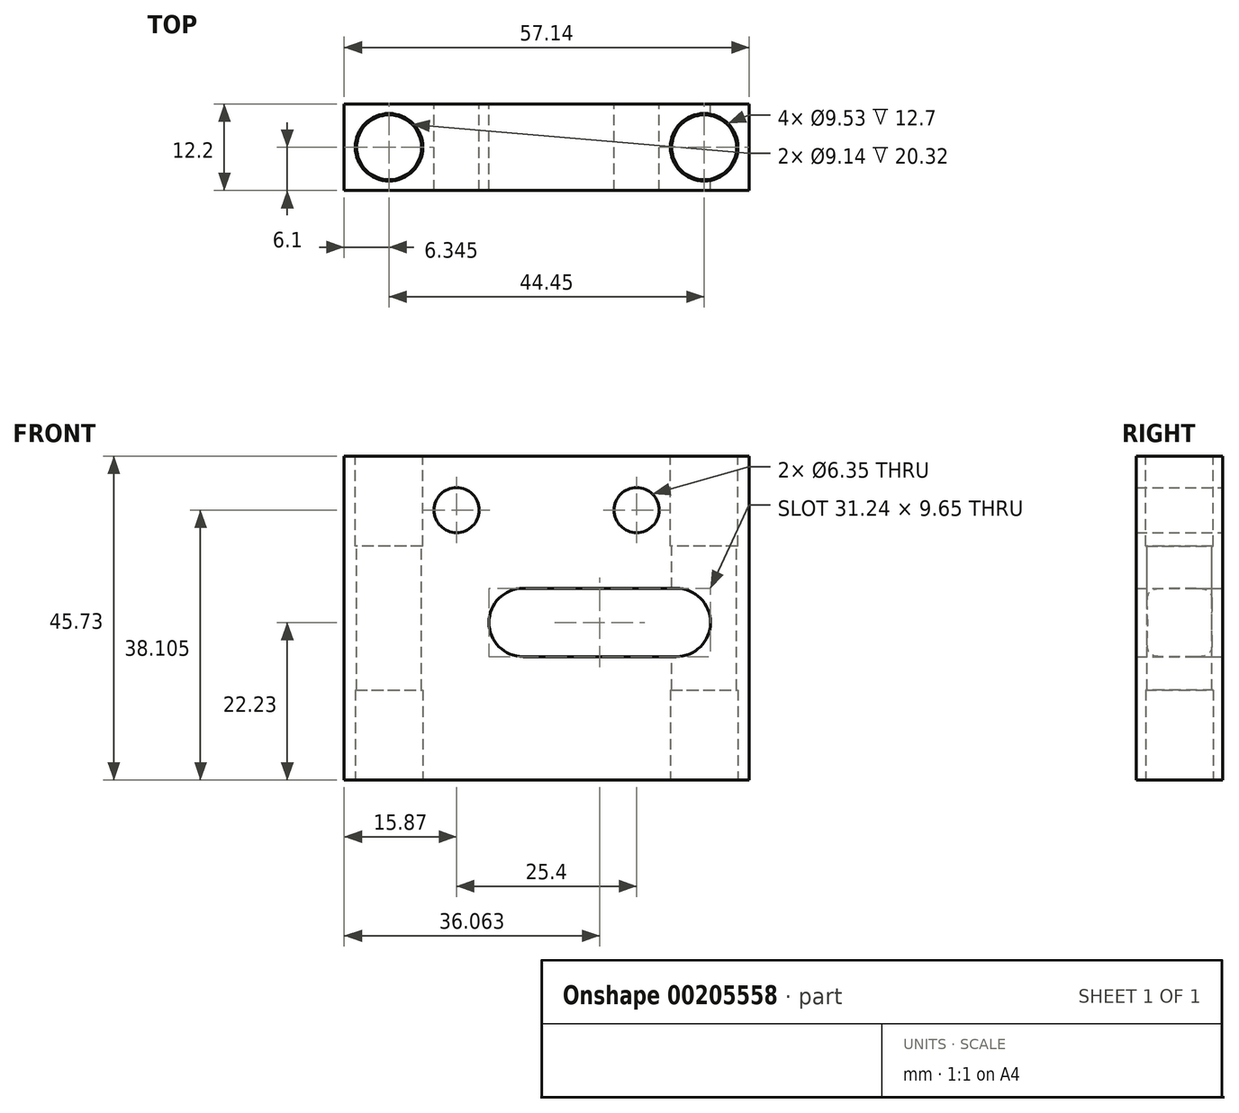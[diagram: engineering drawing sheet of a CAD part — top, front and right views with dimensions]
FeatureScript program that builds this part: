
annotation { "Feature Type Name" : "Feature", "Feature Type Description" : "" }
export const myFeature = defineFeature(function(context is Context, id is Id, definition is map)
    precondition{}
    {
        {
            var Q0;
            Q0=qCreatedBy(makeId("Front.planeOp"),FACE);
            var sketch = newSketch(context, id + "F0", { "sketchPlane" : qUnion([Q0])});
            skPoint(sketch, "E0.middle", {"position": v(0, 0) * mm});
            skCircle(sketch, "E1", {"center": v(-12.7, 15.88) * mm, "radius": 3.18 * mm});
            skCircle(sketch, "E2", {"center": v(12.7, 15.88) * mm, "radius": 3.18 * mm});
            skLineSegment(sketch, "E3", {"start": v(-3.3, 4.83) * mm, "end": v(18.29, 4.83) * mm});
            skLineSegment(sketch, "E4", {"start": v(-3.3, -4.83) * mm, "end": v(18.29, -4.83) * mm});
            skLineSegment(sketch, "E5", {"start": v(-28.57, 23.5) * mm, "end": v(28.58, 23.5) * mm});
            skLineSegment(sketch, "E6", {"start": v(-28.57, 23.5) * mm, "end": v(-28.57, -22.23) * mm});
            skLineSegment(sketch, "E7", {"start": v(-28.57, -22.23) * mm, "end": v(28.58, -22.22) * mm});
            skLineSegment(sketch, "E8", {"start": v(28.58, -22.22) * mm, "end": v(28.58, 23.5) * mm});
            skArc(sketch, "E9", {"start": v(-3.3, 4.83) * mm, "mid": v(-8.13, 0) * mm, "end": v(-3.3, -4.83) * mm});
            skArc(sketch, "E10", {"start": v(18.29, -4.83) * mm, "mid": v(23.11, 0) * mm, "end": v(18.29, 4.83) * mm});
            skSolve(sketch);
        }
        {
            var Q0;
            Q0=qSketchRegion(id+"F0",true);
            extrude(context, id + "F1", {"entities" : qUnion([Q0]), "depth" : 12.2 * mm, "symmetric" : true});
        }
        {
            var Q0;
            Q0=makeQuery(id+"F1.opExtrude","SWEPT_FACE",FACE,{"disambiguationData":[OSD([sQuery(id+"F0.wireOp",EDGE,"E5")])]});
            var sketch = newSketch(context, id + "F2", { "sketchPlane" : qUnion([Q0])});
            skCircle(sketch, "E11", {"center": v(-22.23, 0) * mm, "radius": 4.57 * mm});
            skCircle(sketch, "E12", {"center": v(22.23, 0) * mm, "radius": 4.57 * mm});
            skSolve(sketch);
        }
        {
            var Q0;
            Q0=qSketchRegion(id+"F2",true);
            extrude(context, id + "F3", {"entities" : qUnion([Q0]), "operationType" : NewBodyOperationType.REMOVE, "endBound" : BoundingType.THROUGH_ALL, "oppositeDirection" : true, "depth" : 25.4 * mm});
        }
        {
            var Q0;
            Q0=makeQuery(id+"F1.opExtrude","SWEPT_FACE",FACE,{"disambiguationData":[OSD([sQuery(id+"F0.wireOp",EDGE,"E5")])]});
            var sketch = newSketch(context, id + "F4", { "sketchPlane" : qUnion([Q0])});
            skCircle(sketch, "E13", {"center": v(-22.23, 0) * mm, "radius": 4.76 * mm});
            skCircle(sketch, "E14", {"center": v(22.23, 0) * mm, "radius": 4.76 * mm});
            skSolve(sketch);
        }
        {
            var Q0;
            Q0=qSketchRegion(id+"F4",true);
            extrude(context, id + "F5", {"entities" : qUnion([Q0]), "operationType" : NewBodyOperationType.REMOVE, "flatOperationType" : FlatOperationType.REMOVE, "oppositeDirection" : true, "offsetDistance" : 25.4 * mm, "depth" : 12.7 * mm, "domain" : OperationDomain.MODEL});
        }
        {
            var Q0;
            Q0=makeQuery(id+"F1.opExtrude","SWEPT_FACE",FACE,{"disambiguationData":[OSD([sQuery(id+"F0.wireOp",EDGE,"E7")])]});
            var sketch = newSketch(context, id + "F6", { "sketchPlane" : qUnion([Q0])});
            skCircle(sketch, "E15", {"center": v(22.22, 0) * mm, "radius": 4.76 * mm});
            skCircle(sketch, "E16", {"center": v(-22.23, 0) * mm, "radius": 4.76 * mm});
            skSolve(sketch);
        }
        {
            var Q0;
            Q0=qSketchRegion(id+"F6",true);
            extrude(context, id + "F7", {"entities" : qUnion([Q0]), "operationType" : NewBodyOperationType.REMOVE, "oppositeDirection" : true, "depth" : 12.7 * mm});
        }
    });
